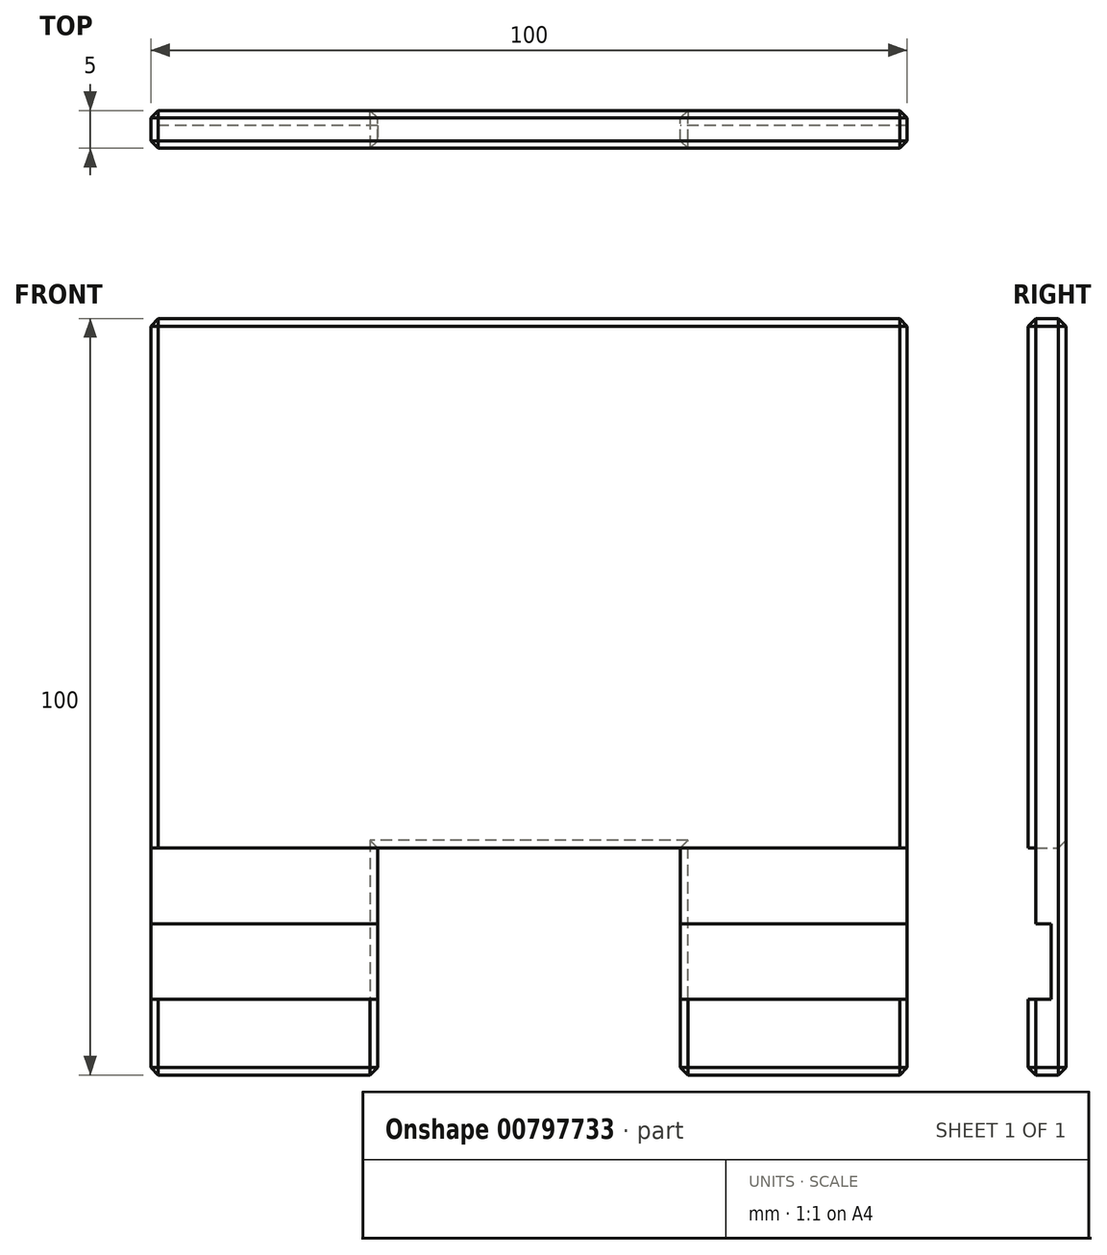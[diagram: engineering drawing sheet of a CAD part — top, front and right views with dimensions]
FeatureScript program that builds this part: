
annotation { "Feature Type Name" : "Feature", "Feature Type Description" : "" }
export const myFeature = defineFeature(function(context is Context, id is Id, definition is map)
    precondition{}
    {
        {
            var Q0;
            Q0=qCreatedBy(makeId("Front.planeOp"),FACE);
            var sketch = newSketch(context, id + "F0", { "sketchPlane" : qUnion([Q0])});
            skLineSegment(sketch, "E0.bottom", {"start": v(66.33, 49.74) * mm, "end": v(-33.67, 49.74) * mm});
            skLineSegment(sketch, "E0.top", {"start": v(66.33, -50.26) * mm, "end": v(36.33, -50.26) * mm});
            skLineSegment(sketch, "E0.left", {"start": v(66.33, 49.74) * mm, "end": v(66.33, -50.26) * mm});
            skLineSegment(sketch, "E0.right", {"start": v(-33.67, 49.74) * mm, "end": v(-33.67, -50.26) * mm});
            skLineSegment(sketch, "E1", {"start": v(66.33, -50.26) * mm, "end": v(36.33, -50.26) * mm, "construction": true});
            skLineSegment(sketch, "E2", {"start": v(16.33, 49.74) * mm, "end": v(16.33, -50.26) * mm, "construction": true});
            skLineSegment(sketch, "E3", {"start": v(36.33, -50.26) * mm, "end": v(36.33, -20.26) * mm});
            skLineSegment(sketch, "E4", {"start": v(36.33, -20.26) * mm, "end": v(16.33, -20.26) * mm});
            skLineSegment(sketch, "E5.MirrorCS", {"start": v(-3.67, -20.26) * mm, "end": v(16.33, -20.26) * mm});
            skLineSegment(sketch, "E6.MirrorCS", {"start": v(-3.67, -50.26) * mm, "end": v(-3.67, -20.26) * mm});
            skLineSegment(sketch, "E7.trimOffspring", {"start": v(-3.67, -50.26) * mm, "end": v(-33.67, -50.26) * mm});
            skSolve(sketch);
        }
        {
            var Q0;
            Q0 = qSketchRegion(id + "F0", true);
            extrude(context, id + "F1", {"entities" : qUnion([Q0]), "depth" : 5 * mm, "offsetDistance" : 25 * mm});
        }
        {
            var Q0;
            Q0=makeQuery(id+"F1.opExtrude","SWEPT_FACE",FACE,{"disambiguationData":[OSD([sQuery(id+"F0.wireOp",EDGE,"E0.right")])]});
            var sketch = newSketch(context, id + "F2", { "sketchPlane" : qUnion([Q0])});
            skLineSegment(sketch, "E8", {"start": v(5, -40.26) * mm, "end": v(2, -40.26) * mm});
            skLineSegment(sketch, "E9", {"start": v(2, -40.26) * mm, "end": v(2, -30.26) * mm});
            skLineSegment(sketch, "E10", {"start": v(2, -30.26) * mm, "end": v(4, -30.26) * mm});
            skLineSegment(sketch, "E11", {"start": v(4, -30.26) * mm, "end": v(4, -20.26) * mm});
            skLineSegment(sketch, "E12", {"start": v(4, -20.26) * mm, "end": v(5, -20.26) * mm});
            skLineSegment(sketch, "E13", {"start": v(5, -20.26) * mm, "end": v(5, -40.26) * mm});
            skSolve(sketch);
        }
        {
            var Q0;
            Q0 = qSketchRegion(id + "F2", true);
            extrude(context, id + "F3", {"entities" : qUnion([Q0]), "operationType" : NewBodyOperationType.REMOVE, "oppositeDirection" : true, "depth" : 100 * mm, "offsetDistance" : 25 * mm});
        }
        {
            var Q0;
            Q0=makeQuery(id+"F1.opExtrude","CAP_FACE",FACE,{"disambiguationData":[OSD([sQuery(id+"F0.wireOp",EDGE,"E0.bottom"),sQuery(id+"F0.wireOp",EDGE,"E0.top"),sQuery(id+"F0.wireOp",EDGE,"E0.left"),sQuery(id+"F0.wireOp",EDGE,"E0.right"),sQuery(id+"F0.wireOp",EDGE,"E3"),sQuery(id+"F0.wireOp",EDGE,"E4"),sQuery(id+"F0.wireOp",EDGE,"E5.MirrorCS"),sQuery(id+"F0.wireOp",EDGE,"E6.MirrorCS"),sQuery(id+"F0.wireOp",EDGE,"E7.trimOffspring")])],"isStart":true});
            var Q1;
            {var subQ0=sQuery(id+"F0.wireOp",EDGE,"E0.left");var subQ1=sQuery(id+"F0.wireOp",EDGE,"E0.top");Q1=makeQuery(id+"F3.boolean.opBoolean","SPLIT",EDGE,{"disambiguationData":[TD([makeQuery(id+"F1.opExtrude","SWEPT_FACE",FACE,{"disambiguationData":[OSD([subQ1])]})])],"derivedFrom":makeQuery(id+"F1.opExtrude","CAP_EDGE",EDGE,{"disambiguationData":[OSD([subQ0])],"isStart":false})});}
            var Q2;
            Q2=makeQuery(id+"F1.opExtrude","CAP_EDGE",EDGE,{"disambiguationData":[OSD([sQuery(id+"F0.wireOp",EDGE,"E0.top")])],"isStart":false});
            var Q3;
            Q3=makeQuery(id+"F1.opExtrude","CAP_EDGE",EDGE,{"disambiguationData":[OSD([sQuery(id+"F0.wireOp",EDGE,"E3")])],"isStart":false});
            var Q4;
            Q4=makeQuery(id+"F1.opExtrude","CAP_EDGE",EDGE,{"disambiguationData":[OSD([sQuery(id+"F0.wireOp",EDGE,"E6.MirrorCS")])],"isStart":false});
            var Q5;
            Q5=makeQuery(id+"F1.opExtrude","CAP_EDGE",EDGE,{"disambiguationData":[OSD([sQuery(id+"F0.wireOp",EDGE,"E7.trimOffspring")])],"isStart":false});
            var Q6;
            {var subQ0=sQuery(id+"F0.wireOp",EDGE,"E7.trimOffspring");var subQ1=sQuery(id+"F0.wireOp",EDGE,"E0.right");Q6=makeQuery(id+"F3.boolean.opBoolean","SPLIT",EDGE,{"disambiguationData":[TD([makeQuery(id+"F1.opExtrude","SWEPT_FACE",FACE,{"disambiguationData":[OSD([subQ0])]})])],"derivedFrom":makeQuery(id+"F1.opExtrude","CAP_EDGE",EDGE,{"disambiguationData":[OSD([subQ1])],"isStart":false})});}
            var Q7;
            Q7=makeQuery(id+"F1.opExtrude","SWEPT_EDGE",EDGE,{"disambiguationData":[OSD([sQuery(id+"F0.wireOp",EDGE,"E0.top"),sQuery(id+"F0.wireOp",EDGE,"E0.left")])]});
            var Q8;
            Q8=makeQuery(id+"F1.opExtrude","SWEPT_EDGE",EDGE,{"disambiguationData":[OSD([sQuery(id+"F0.wireOp",EDGE,"E0.top"),sQuery(id+"F0.wireOp",EDGE,"E3")])]});
            var Q9;
            Q9=makeQuery(id+"F1.opExtrude","SWEPT_EDGE",EDGE,{"disambiguationData":[OSD([sQuery(id+"F0.wireOp",EDGE,"E6.MirrorCS"),sQuery(id+"F0.wireOp",EDGE,"E7.trimOffspring")])]});
            var Q10;
            Q10=makeQuery(id+"F1.opExtrude","SWEPT_EDGE",EDGE,{"disambiguationData":[OSD([sQuery(id+"F0.wireOp",EDGE,"E0.right"),sQuery(id+"F0.wireOp",EDGE,"E7.trimOffspring")])]});
            var Q11;
            Q11=makeQuery(id+"F1.opExtrude","SWEPT_EDGE",EDGE,{"disambiguationData":[OSD([sQuery(id+"F0.wireOp",EDGE,"E0.bottom"),sQuery(id+"F0.wireOp",EDGE,"E0.right")])]});
            var Q12;
            Q12=makeQuery(id+"F1.opExtrude","SWEPT_EDGE",EDGE,{"disambiguationData":[OSD([sQuery(id+"F0.wireOp",EDGE,"E0.bottom"),sQuery(id+"F0.wireOp",EDGE,"E0.left")])]});
            var Q13;
            {var subQ2=sQuery(id+"F0.wireOp",EDGE,"E0.right");var subQ3=sQuery(id+"F0.wireOp",EDGE,"E0.bottom");Q13=makeQuery(id+"F3.boolean.opBoolean","SPLIT",EDGE,{"disambiguationData":[TD([makeQuery(id+"F1.opExtrude","SWEPT_FACE",FACE,{"disambiguationData":[OSD([subQ3])]})])],"derivedFrom":makeQuery(id+"F1.opExtrude","CAP_EDGE",EDGE,{"disambiguationData":[OSD([subQ2])],"isStart":false})});}
            var Q14;
            Q14=makeQuery(id+"F1.opExtrude","CAP_EDGE",EDGE,{"disambiguationData":[OSD([sQuery(id+"F0.wireOp",EDGE,"E0.bottom")])],"isStart":false});
            var Q15;
            {var subQ0=sQuery(id+"F0.wireOp",EDGE,"E0.left");var subQ3=sQuery(id+"F0.wireOp",EDGE,"E0.bottom");Q15=makeQuery(id+"F3.boolean.opBoolean","SPLIT",EDGE,{"disambiguationData":[TD([makeQuery(id+"F1.opExtrude","SWEPT_FACE",FACE,{"disambiguationData":[OSD([subQ3])]})])],"derivedFrom":makeQuery(id+"F1.opExtrude","CAP_EDGE",EDGE,{"disambiguationData":[OSD([subQ0])],"isStart":false})});}
            chamfer(context, id + "F4", {"entities" : qUnion([Q0, Q1, Q2, Q3, Q4, Q5, Q6, Q7, Q8, Q9, Q10, Q11, Q12, Q13, Q14, Q15]), "width" : 1 * mm, "tangentPropagation" : true});
        }
    });
